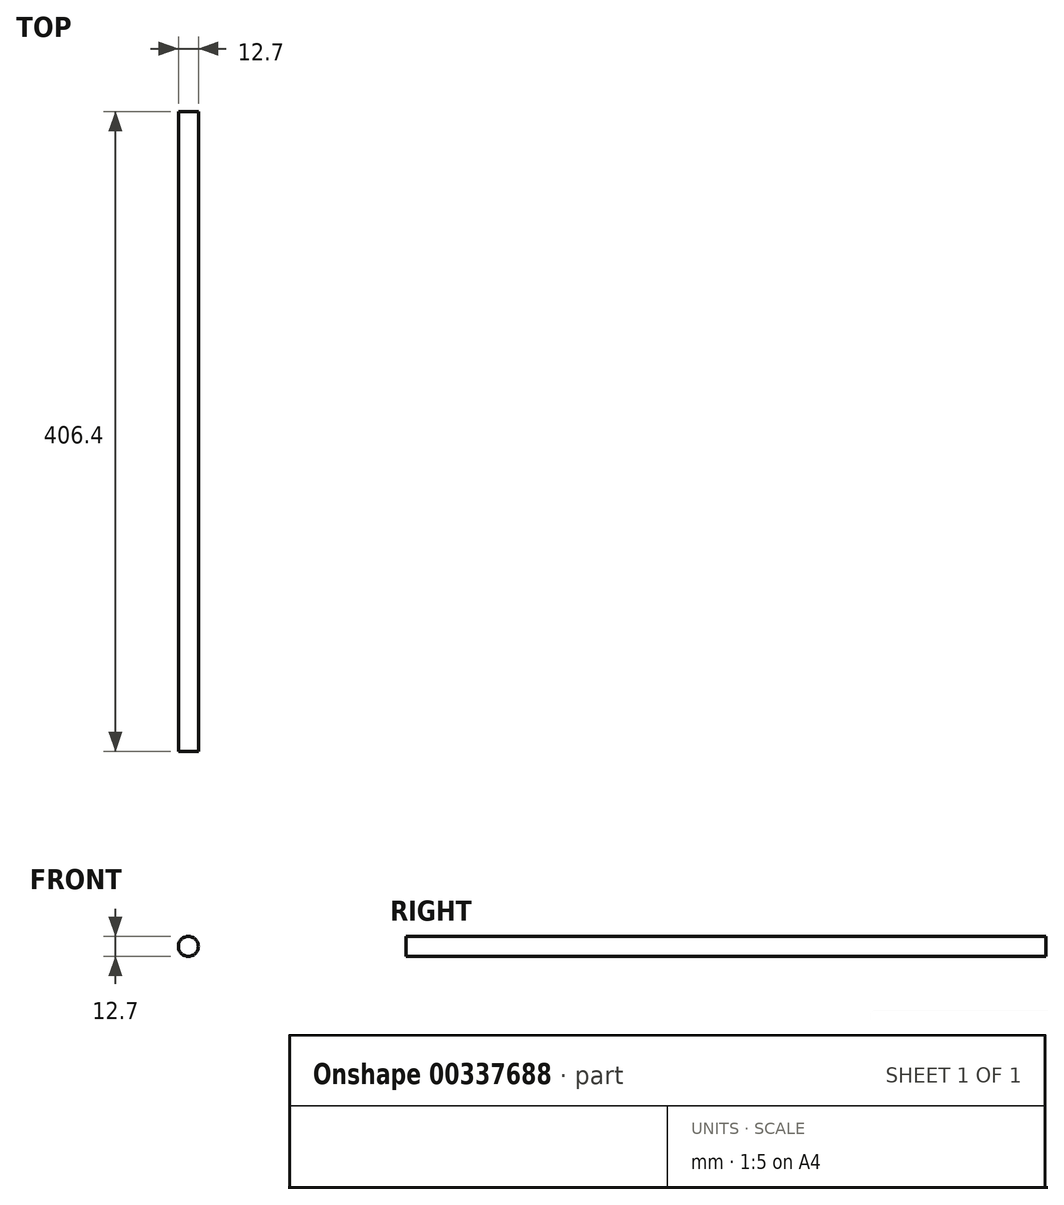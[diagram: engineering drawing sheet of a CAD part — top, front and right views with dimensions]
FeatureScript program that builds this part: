
annotation { "Feature Type Name" : "Feature", "Feature Type Description" : "" }
export const myFeature = defineFeature(function(context is Context, id is Id, definition is map)
    precondition{}
    {
        {
            var Q0;
            Q0=qCreatedBy(makeId("Front.planeOp"),FACE);
            var sketch = newSketch(context, id + "F0", { "sketchPlane" : qUnion([Q0])});
            skCircle(sketch, "E0", {"center": v(0, 0) * mm, "radius": 6.35 * mm});
            skSolve(sketch);
        }
        {
            var Q0;
            Q0=makeQuery(id+"F0.imprint","IMPRINT",FACE,{"disambiguationData":[TD([[makeQuery(id+"F0.imprint","IMPRINT",EDGE,{"derivedFrom":sQuery(id+"F0.wireOp",EDGE,"E0")}),1.0]])]});
            extrude(context, id + "F1", {"entities" : qUnion([Q0]), "depth" : 406.4 * mm});
        }
    });
